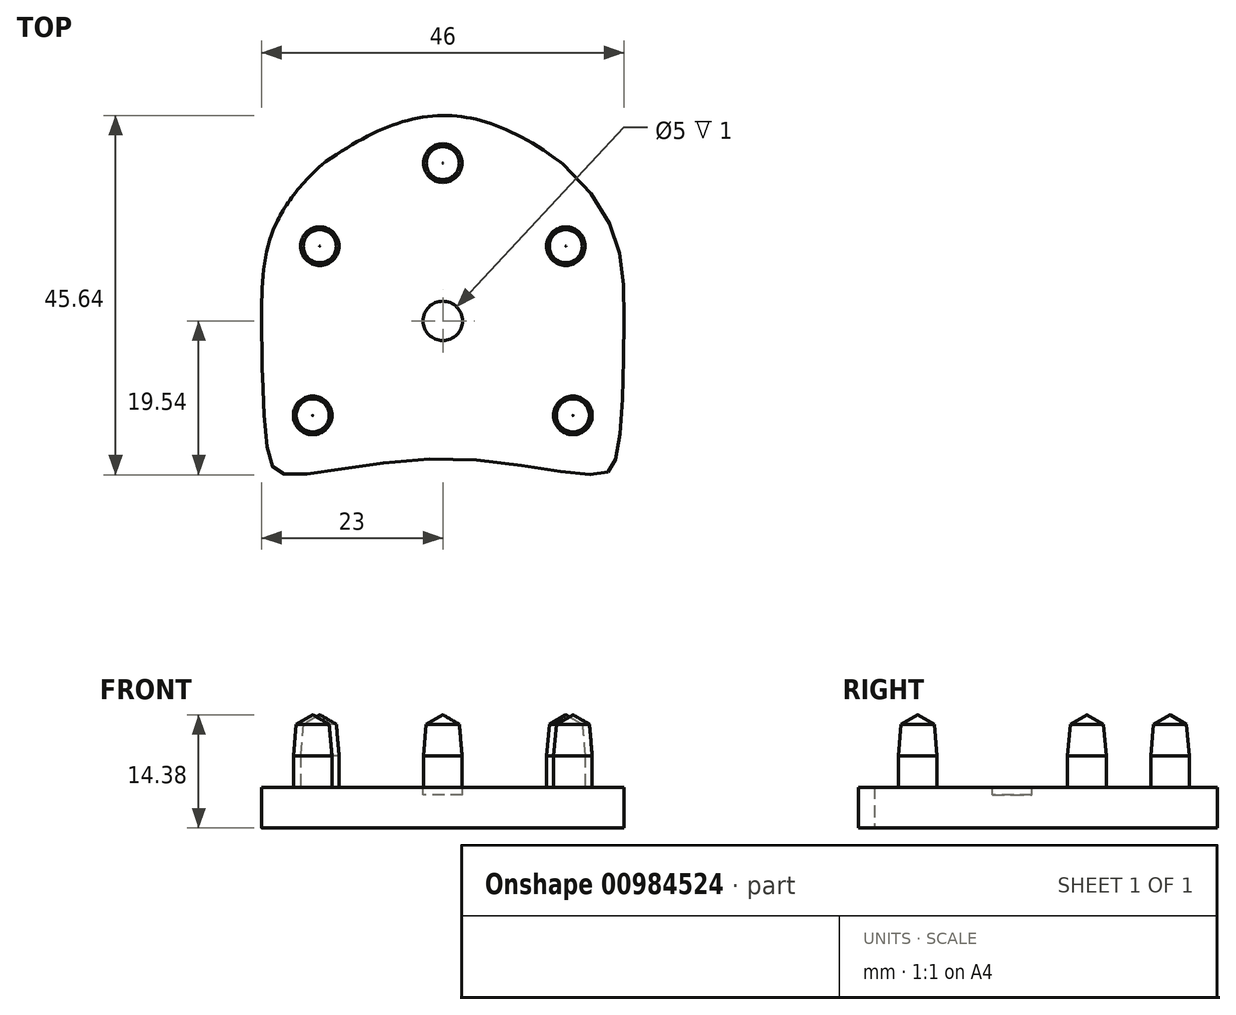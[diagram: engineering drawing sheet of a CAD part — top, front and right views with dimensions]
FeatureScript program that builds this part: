
annotation { "Feature Type Name" : "Feature", "Feature Type Description" : "" }
export const myFeature = defineFeature(function(context is Context, id is Id, definition is map)
    precondition{}
    {
        {
            var Q0;
            Q0=qCreatedBy(makeId("Top.planeOp"),FACE);
            var sketch = newSketch(context, id + "F0", { "sketchPlane" : qUnion([Q0])});
            skCircle(sketch, "E0", {"center": v(0, 0) * mm, "radius": 2.5 * mm});
            skLineSegment(sketch, "E1", {"start": v(0, -2.5) * mm, "end": v(0, -17.5) * mm, "construction": true});
            skLineSegment(sketch, "E2", {"start": v(0, 2.5) * mm, "end": v(0, 26.5) * mm, "construction": true});
            skLineSegment(sketch, "E3", {"start": v(-23, 0) * mm, "end": v(23, 0) * mm, "construction": true});
            skLineSegment(sketch, "E4", {"start": v(-20, -17.5) * mm, "end": v(20, -17.5) * mm, "construction": true});
            skLineSegment(sketch, "E5", {"start": v(-20, -17.5) * mm, "end": v(-20, -19.5) * mm, "construction": true});
            skLineSegment(sketch, "E6", {"start": v(20, -17.5) * mm, "end": v(20, -19.5) * mm, "construction": true});
            skFitSpline(sketch, "E7", {"points": [v(-20, -19.5) * mm, v(-22, -17.5) * mm, v(-23, 0) * mm, v(-20, 14.5) * mm, v(0, 26.5) * mm, v(20, 14.5) * mm, v(23, 0) * mm, v(22, -17.5) * mm, v(20, -19.5) * mm, v(0, -17.5) * mm, v(-20, -19.5) * mm]});
            skLineSegment(sketch, "E8", {"start": v(0, 14.5) * mm, "end": v(-20, 14.5) * mm, "construction": true});
            skLineSegment(sketch, "E9", {"start": v(0, 14.5) * mm, "end": v(20, 14.5) * mm, "construction": true});
            skLineSegment(sketch, "E10", {"start": v(-16.53, -12) * mm, "end": v(16.53, -12) * mm});
            skLineSegment(sketch, "E11", {"start": v(0, -12) * mm, "end": v(0, 0) * mm});
            skLineSegment(sketch, "E12", {"start": v(0, 0) * mm, "end": v(0, 9.5) * mm});
            skLineSegment(sketch, "E13", {"start": v(-15.62, 9.5) * mm, "end": v(15.62, 9.5) * mm});
            skCircle(sketch, "E14", {"center": v(-16.53, -12) * mm, "radius": 2.45 * mm});
            skCircle(sketch, "E15", {"center": v(-15.62, 9.5) * mm, "radius": 2.45 * mm});
            skCircle(sketch, "E16", {"center": v(15.62, 9.5) * mm, "radius": 2.45 * mm});
            skCircle(sketch, "E17", {"center": v(16.53, -12) * mm, "radius": 2.45 * mm});
            skCircle(sketch, "E18", {"center": v(0, 20.05) * mm, "radius": 2.45 * mm});
            skLineSegment(sketch, "E19", {"start": v(-22.62, -18.33) * mm, "end": v(-22.97, -5.02) * mm});
            skLineSegment(sketch, "E20", {"start": v(-24.2, 5.99) * mm, "end": v(-18.81, 17.38) * mm});
            skFitSpline(sketch, "E21", {"points": [v(-15.12, 20.05) * mm, v(15.12, 20.05) * mm], "startDerivative": vector(30.63, 21.43) * mm, "endDerivative": vector(35.85, -26.83) * mm});
            skLineSegment(sketch, "E22", {"start": v(0, 26.5) * mm, "end": v(0, 26.1) * mm});
            skSolve(sketch);
        }
        {
            var Q0;
            Q0=makeQuery(id+"F0.imprint","IMPRINT",FACE,{"disambiguationData":[TD([[makeQuery(id+"F0.imprint","IMPRINT",EDGE,{"derivedFrom":sQuery(id+"F0.wireOp",EDGE,"E16")}),1.0]])]});
            var Q1;
            {var subQ0=sQuery(id+"F0.wireOp",EDGE,"E11");var subQ1=sQuery(id+"F0.wireOp",EDGE,"E0");var subQ2=makeQuery(id+"F0.imprint","INTERSECT",VERTEX,{"derivedFrom":[subQ1,subQ0]});Q1=makeQuery(id+"F0.imprint","IMPRINT",FACE,{"disambiguationData":[TD([[makeQuery(id+"F0.imprint","IMPRINT",EDGE,{"disambiguationData":[TD([[subQ2,1.0]])],"derivedFrom":subQ1}),1.0]])]});}
            var Q2;
            Q2=makeQuery(id+"F0.imprint","IMPRINT",FACE,{"disambiguationData":[TD([[makeQuery(id+"F0.imprint","IMPRINT",EDGE,{"derivedFrom":sQuery(id+"F0.wireOp",EDGE,"E18")}),1.0]])]});
            var Q3;
            Q3=makeQuery(id+"F0.imprint","IMPRINT",FACE,{"disambiguationData":[TD([[makeQuery(id+"F0.imprint","IMPRINT",EDGE,{"derivedFrom":sQuery(id+"F0.wireOp",EDGE,"E14")}),1.0]])]});
            var Q4;
            Q4=makeQuery(id+"F0.imprint","IMPRINT",FACE,{"disambiguationData":[TD([[makeQuery(id+"F0.imprint","IMPRINT",EDGE,{"derivedFrom":sQuery(id+"F0.wireOp",EDGE,"E17")}),1.0]])]});
            var Q5;
            {var subQ0=sQuery(id+"F0.wireOp",EDGE,"E11");var subQ1=sQuery(id+"F0.wireOp",EDGE,"E0");var subQ2=makeQuery(id+"F0.imprint","INTERSECT",VERTEX,{"derivedFrom":[subQ1,subQ0]});Q5=makeQuery(id+"F0.imprint","IMPRINT",FACE,{"disambiguationData":[TD([[makeQuery(id+"F0.imprint","IMPRINT",EDGE,{"disambiguationData":[TD([[subQ2,-1.0]])],"derivedFrom":subQ1}),1.0]])]});}
            var Q6;
            Q6=makeQuery(id+"F0.imprint","IMPRINT",FACE,{"disambiguationData":[TD([[makeQuery(id+"F0.imprint","IMPRINT",EDGE,{"derivedFrom":sQuery(id+"F0.wireOp",EDGE,"E15")}),1.0]])]});
            var Q7;
            Q7=makeQuery(id+"F0.imprint","IMPRINT",FACE,{"disambiguationData":[TD([[makeQuery(id+"F0.imprint","IMPRINT",EDGE,{"derivedFrom":sQuery(id+"F0.wireOp",EDGE,"E14")}),-1.0]])]});
            extrude(context, id + "F1", {"entities" : qUnion([Q0, Q1, Q2, Q3, Q4, Q5, Q6, Q7]), "oppositeDirection" : true, "depth" : 5.18 * mm, "offsetDistance" : 25 * mm});
        }
        {
            var Q0;
            Q0=makeQuery(id+"F0.imprint","IMPRINT",FACE,{"disambiguationData":[TD([[makeQuery(id+"F0.imprint","IMPRINT",EDGE,{"derivedFrom":sQuery(id+"F0.wireOp",EDGE,"E15")}),1.0]])]});
            var Q1;
            Q1=makeQuery(id+"F0.imprint","IMPRINT",FACE,{"disambiguationData":[TD([[makeQuery(id+"F0.imprint","IMPRINT",EDGE,{"derivedFrom":sQuery(id+"F0.wireOp",EDGE,"E18")}),1.0]])]});
            var Q2;
            Q2=makeQuery(id+"F0.imprint","IMPRINT",FACE,{"disambiguationData":[TD([[makeQuery(id+"F0.imprint","IMPRINT",EDGE,{"derivedFrom":sQuery(id+"F0.wireOp",EDGE,"E16")}),1.0]])]});
            var Q3;
            Q3=makeQuery(id+"F0.imprint","IMPRINT",FACE,{"disambiguationData":[TD([[makeQuery(id+"F0.imprint","IMPRINT",EDGE,{"derivedFrom":sQuery(id+"F0.wireOp",EDGE,"E17")}),1.0]])]});
            var Q4;
            Q4=makeQuery(id+"F0.imprint","IMPRINT",FACE,{"disambiguationData":[TD([[makeQuery(id+"F0.imprint","IMPRINT",EDGE,{"derivedFrom":sQuery(id+"F0.wireOp",EDGE,"E14")}),1.0]])]});
            extrude(context, id + "F2", {"entities" : qUnion([Q0, Q1, Q2, Q3, Q4]), "operationType" : NewBodyOperationType.ADD, "depth" : 4 * mm, "offsetDistance" : 25 * mm});
        }
        {
            var Q0;
            {var subQ0=sQuery(id+"F0.wireOp",EDGE,"E11");var subQ1=sQuery(id+"F0.wireOp",EDGE,"E0");var subQ2=makeQuery(id+"F0.imprint","INTERSECT",VERTEX,{"derivedFrom":[subQ1,subQ0]});Q0=makeQuery(id+"F0.imprint","IMPRINT",FACE,{"disambiguationData":[TD([[makeQuery(id+"F0.imprint","IMPRINT",EDGE,{"disambiguationData":[TD([[subQ2,1.0]])],"derivedFrom":subQ1}),1.0]])]});}
            var Q1;
            {var subQ0=sQuery(id+"F0.wireOp",EDGE,"E11");var subQ1=sQuery(id+"F0.wireOp",EDGE,"E0");var subQ2=makeQuery(id+"F0.imprint","INTERSECT",VERTEX,{"derivedFrom":[subQ1,subQ0]});Q1=makeQuery(id+"F0.imprint","IMPRINT",FACE,{"disambiguationData":[TD([[makeQuery(id+"F0.imprint","IMPRINT",EDGE,{"disambiguationData":[TD([[subQ2,-1.0]])],"derivedFrom":subQ1}),1.0]])]});}
            extrude(context, id + "F3", {"entities" : qUnion([Q0, Q1]), "operationType" : NewBodyOperationType.REMOVE, "oppositeDirection" : true, "depth" : 1 * mm, "offsetDistance" : 25 * mm});
        }
        {
            var Q0;
            Q0=makeQuery(id+"F2.opExtrude","CAP_FACE",FACE,{"disambiguationData":[OSD([sQuery(id+"F0.wireOp",EDGE,"E14")])],"isStart":false});
            var Q1;
            Q1=makeQuery(id+"F2.opExtrude","CAP_FACE",FACE,{"disambiguationData":[OSD([sQuery(id+"F0.wireOp",EDGE,"E15")])],"isStart":false});
            var Q2;
            Q2=makeQuery(id+"F2.opExtrude","CAP_FACE",FACE,{"disambiguationData":[OSD([sQuery(id+"F0.wireOp",EDGE,"E18")])],"isStart":false});
            var Q3;
            Q3=makeQuery(id+"F2.opExtrude","CAP_FACE",FACE,{"disambiguationData":[OSD([sQuery(id+"F0.wireOp",EDGE,"E16")])],"isStart":false});
            var Q4;
            Q4=makeQuery(id+"F2.opExtrude","CAP_FACE",FACE,{"disambiguationData":[OSD([sQuery(id+"F0.wireOp",EDGE,"E17")])],"isStart":false});
            extrude(context, id + "F4", {"entities" : qUnion([Q0, Q1, Q2, Q3, Q4]), "operationType" : NewBodyOperationType.ADD, "depth" : 4 * mm, "offsetDistance" : 25 * mm, "hasDraft" : true, "draftAngle" : 5 * degree, "draftPullDirection" : true});
        }
        {
            var Q0;
            Q0=makeQuery(id+"F4.opExtrude","CAP_FACE",FACE,{"disambiguationData":[OSD([sQuery(id+"F0.wireOp",EDGE,"E14")])],"isStart":false});
            var Q1;
            Q1=makeQuery(id+"F4.opExtrude","CAP_FACE",FACE,{"disambiguationData":[OSD([sQuery(id+"F0.wireOp",EDGE,"E15")])],"isStart":false});
            var Q2;
            Q2=makeQuery(id+"F4.opExtrude","CAP_FACE",FACE,{"disambiguationData":[OSD([sQuery(id+"F0.wireOp",EDGE,"E18")])],"isStart":false});
            var Q3;
            Q3=makeQuery(id+"F4.opExtrude","CAP_FACE",FACE,{"disambiguationData":[OSD([sQuery(id+"F0.wireOp",EDGE,"E16")])],"isStart":false});
            var Q4;
            Q4=makeQuery(id+"F4.opExtrude","CAP_FACE",FACE,{"disambiguationData":[OSD([sQuery(id+"F0.wireOp",EDGE,"E17")])],"isStart":false});
            extrude(context, id + "F5", {"entities" : qUnion([Q0, Q1, Q2, Q3, Q4]), "operationType" : NewBodyOperationType.ADD, "depth" : 1.2 * mm, "offsetDistance" : 25 * mm, "hasDraft" : true, "draftAngle" : 60 * degree, "draftPullDirection" : true});
        }
        {
            var Q0;
            {var subQ0=sQuery(id+"F0.wireOp",EDGE,"E21");var subQ1=sQuery(id+"F0.wireOp",EDGE,"E7");Q0=makeQuery(id+"F1.opExtrude","SWEPT_EDGE",EDGE,{"disambiguationData":[OSD([subQ1,subQ0]),TDD([makeQuery(id+"F0.imprint","INTERSECT",VERTEX,{"disambiguationData":[OD(0.0)],"derivedFrom":[subQ1,subQ0]})])]});}
            var Q1;
            {var subQ0=sQuery(id+"F0.wireOp",EDGE,"E21");var subQ1=sQuery(id+"F0.wireOp",EDGE,"E7");Q1=makeQuery(id+"F1.opExtrude","SWEPT_EDGE",EDGE,{"disambiguationData":[OSD([subQ1,subQ0]),TDD([makeQuery(id+"F0.imprint","INTERSECT",VERTEX,{"disambiguationData":[OD(1.0)],"derivedFrom":[subQ1,subQ0]})])]});}
            fillet(context, id + "F6", {"entities" : qUnion([Q0, Q1]), "radius" : 5 * mm, "tangentPropagation" : true, "allowEdgeOverflow" : false});
        }
    });
